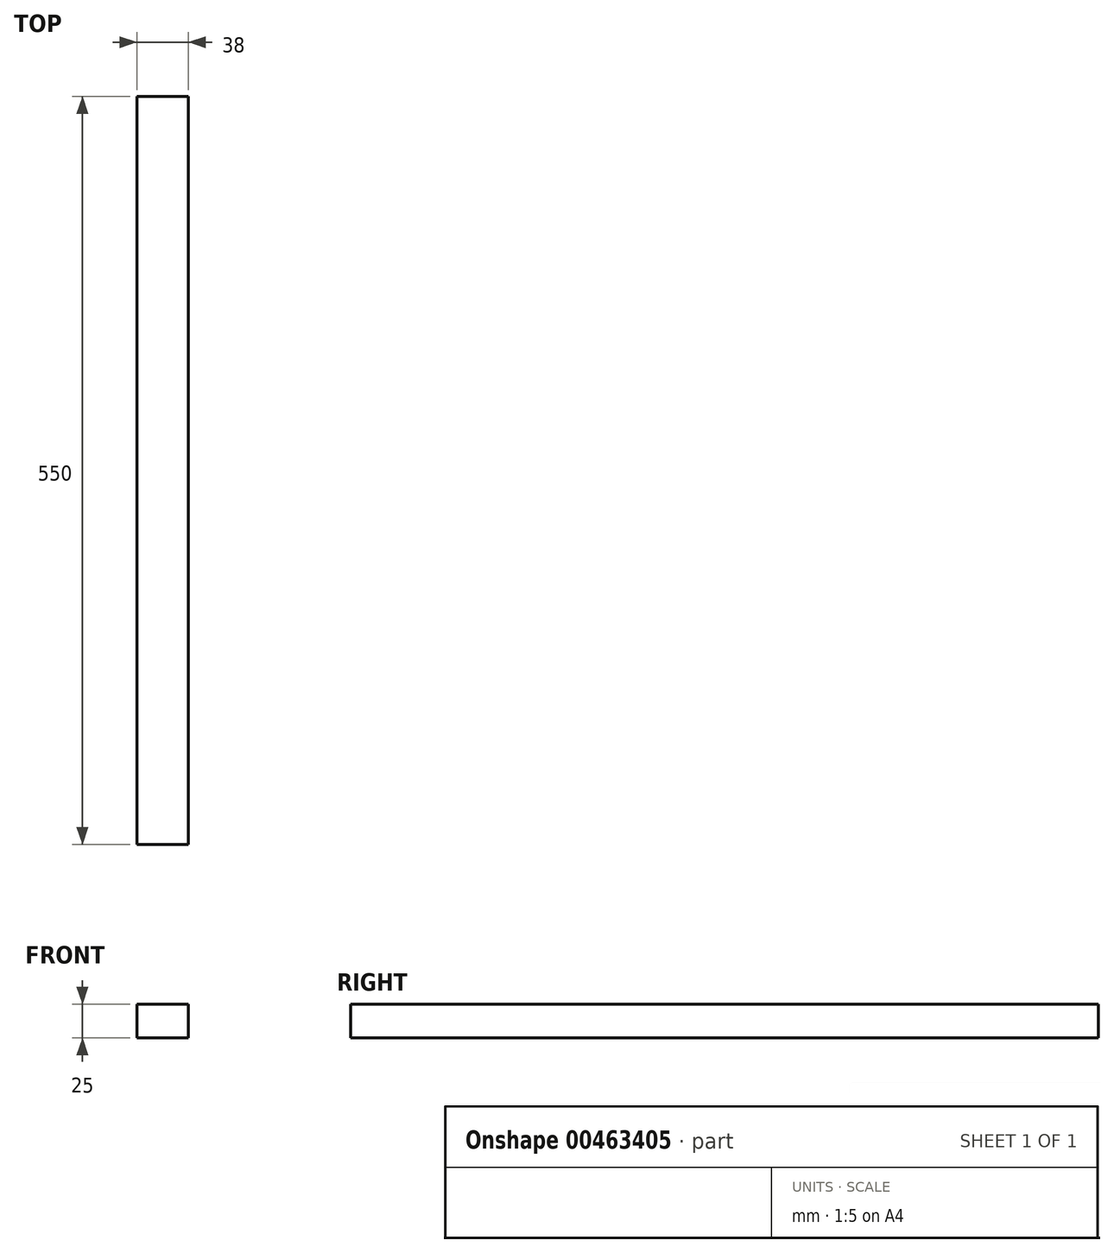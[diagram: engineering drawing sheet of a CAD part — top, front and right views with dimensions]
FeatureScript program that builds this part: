
annotation { "Feature Type Name" : "Feature", "Feature Type Description" : "" }
export const myFeature = defineFeature(function(context is Context, id is Id, definition is map)
    precondition{}
    {
        {
            var Q0;
            Q0=qCreatedBy(makeId("Front.planeOp"),FACE);
            var sketch = newSketch(context, id + "F0", { "sketchPlane" : qUnion([Q0])});
            skLineSegment(sketch, "E0.bottom", {"start": v(0, 0) * mm, "end": v(38, 0) * mm});
            skLineSegment(sketch, "E0.top", {"start": v(0, 25) * mm, "end": v(38, 25) * mm});
            skLineSegment(sketch, "E0.left", {"start": v(0, 25) * mm, "end": v(0, 0) * mm});
            skLineSegment(sketch, "E0.right", {"start": v(38, 25) * mm, "end": v(38, 0) * mm});
            skSolve(sketch);
        }
        {
            var Q0;
            Q0=makeQuery(id+"F0.imprint","IMPRINT",FACE,{"disambiguationData":[TD([[makeQuery(id+"F0.imprint","IMPRINT",EDGE,{"derivedFrom":sQuery(id+"F0.wireOp",EDGE,"E0.bottom")}),1.0]])]});
            extrude(context, id + "F1", {"entities" : qUnion([Q0]), "depth" : 550 * mm});
        }
    });
